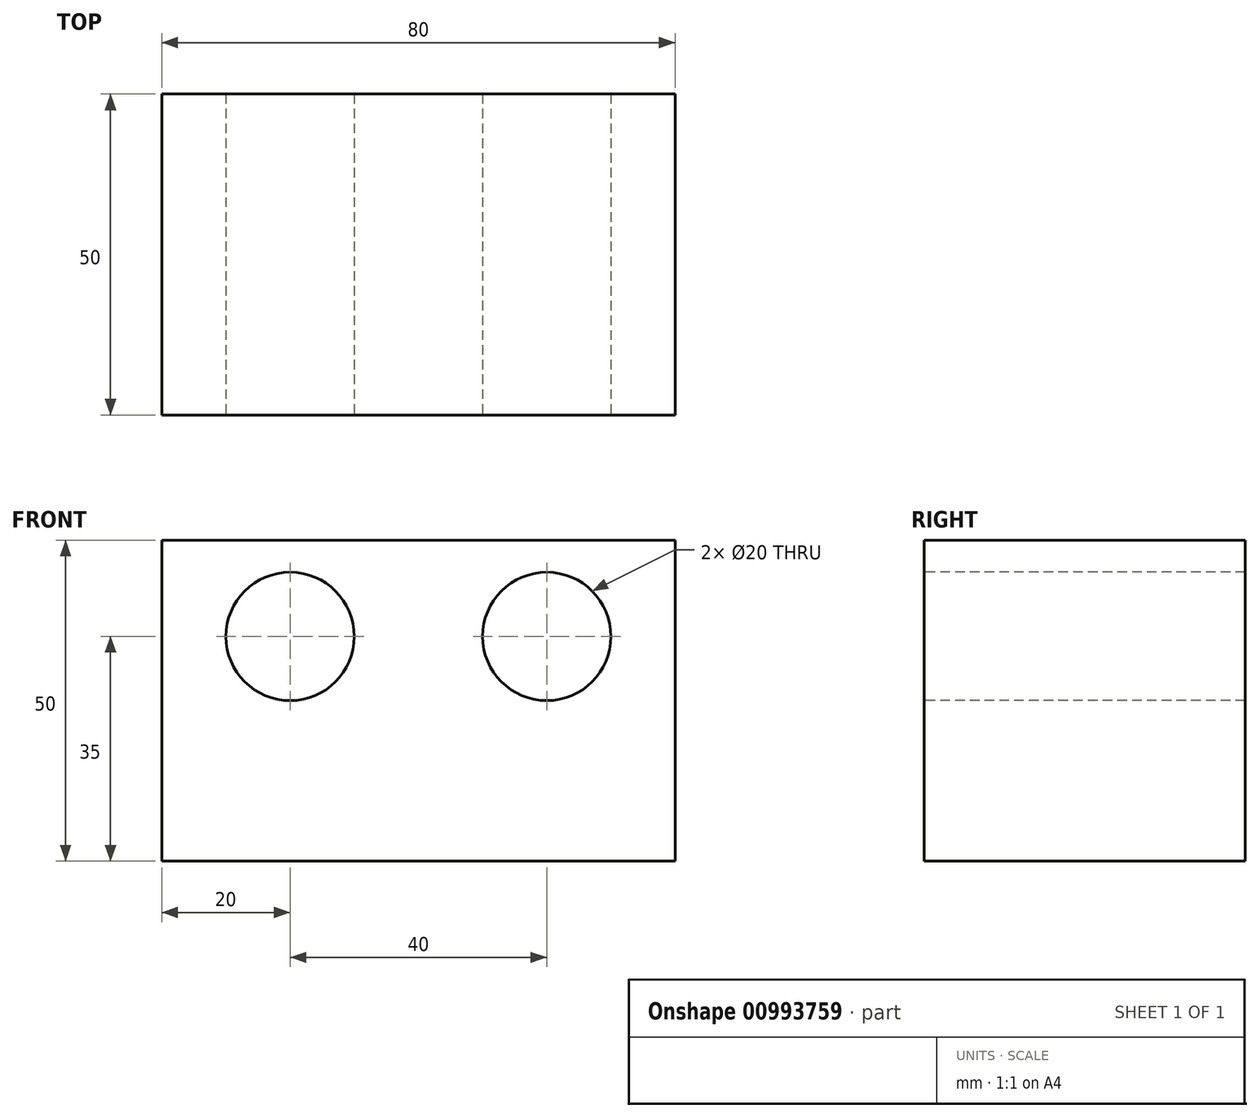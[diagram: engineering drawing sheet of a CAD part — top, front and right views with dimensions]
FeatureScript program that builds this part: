
annotation { "Feature Type Name" : "Feature", "Feature Type Description" : "" }
export const myFeature = defineFeature(function(context is Context, id is Id, definition is map)
    precondition{}
    {
        {
            var Q0;
            Q0=qCreatedBy(makeId("Right.planeOp"),FACE);
            var sketch = newSketch(context, id + "F0", { "sketchPlane" : qUnion([Q0])});
            skLineSegment(sketch, "E0.bottom", {"start": v(-25, 25) * mm, "end": v(25, 25) * mm});
            skLineSegment(sketch, "E0.top", {"start": v(-25, -25) * mm, "end": v(25, -25) * mm});
            skLineSegment(sketch, "E0.left", {"start": v(-25, 25) * mm, "end": v(-25, -25) * mm});
            skLineSegment(sketch, "E0.right", {"start": v(25, 25) * mm, "end": v(25, -25) * mm});
            skPoint(sketch, "E0.middle", {"position": v(0, 0) * mm});
            skSolve(sketch);
        }
        {
            var Q0;
            Q0 = qSketchRegion(id + "F0", true);
            extrude(context, id + "F1", {"entities" : qUnion([Q0]), "oppositeDirection" : true, "depth" : 80 * mm, "offsetDistance" : 25 * mm});
        }
        {
            var Q0;
            Q0=makeQuery(id+"F1.opExtrude","SWEPT_FACE",FACE,{"disambiguationData":[OSD([sQuery(id+"F0.wireOp",EDGE,"E0.left")])]});
            var sketch = newSketch(context, id + "F2", { "sketchPlane" : qUnion([Q0])});
            skCircle(sketch, "E1", {"center": v(-60, 10) * mm, "radius": 10 * mm});
            skCircle(sketch, "E2", {"center": v(-20, 10) * mm, "radius": 10 * mm});
            skSolve(sketch);
        }
        {
            var Q0;
            Q0 = qSketchRegion(id + "F2", true);
            extrude(context, id + "F3", {"entities" : qUnion([Q0]), "operationType" : NewBodyOperationType.REMOVE, "endBound" : BoundingType.UP_TO_NEXT, "oppositeDirection" : true, "depth" : 25 * mm, "offsetDistance" : 25 * mm});
        }
    });
